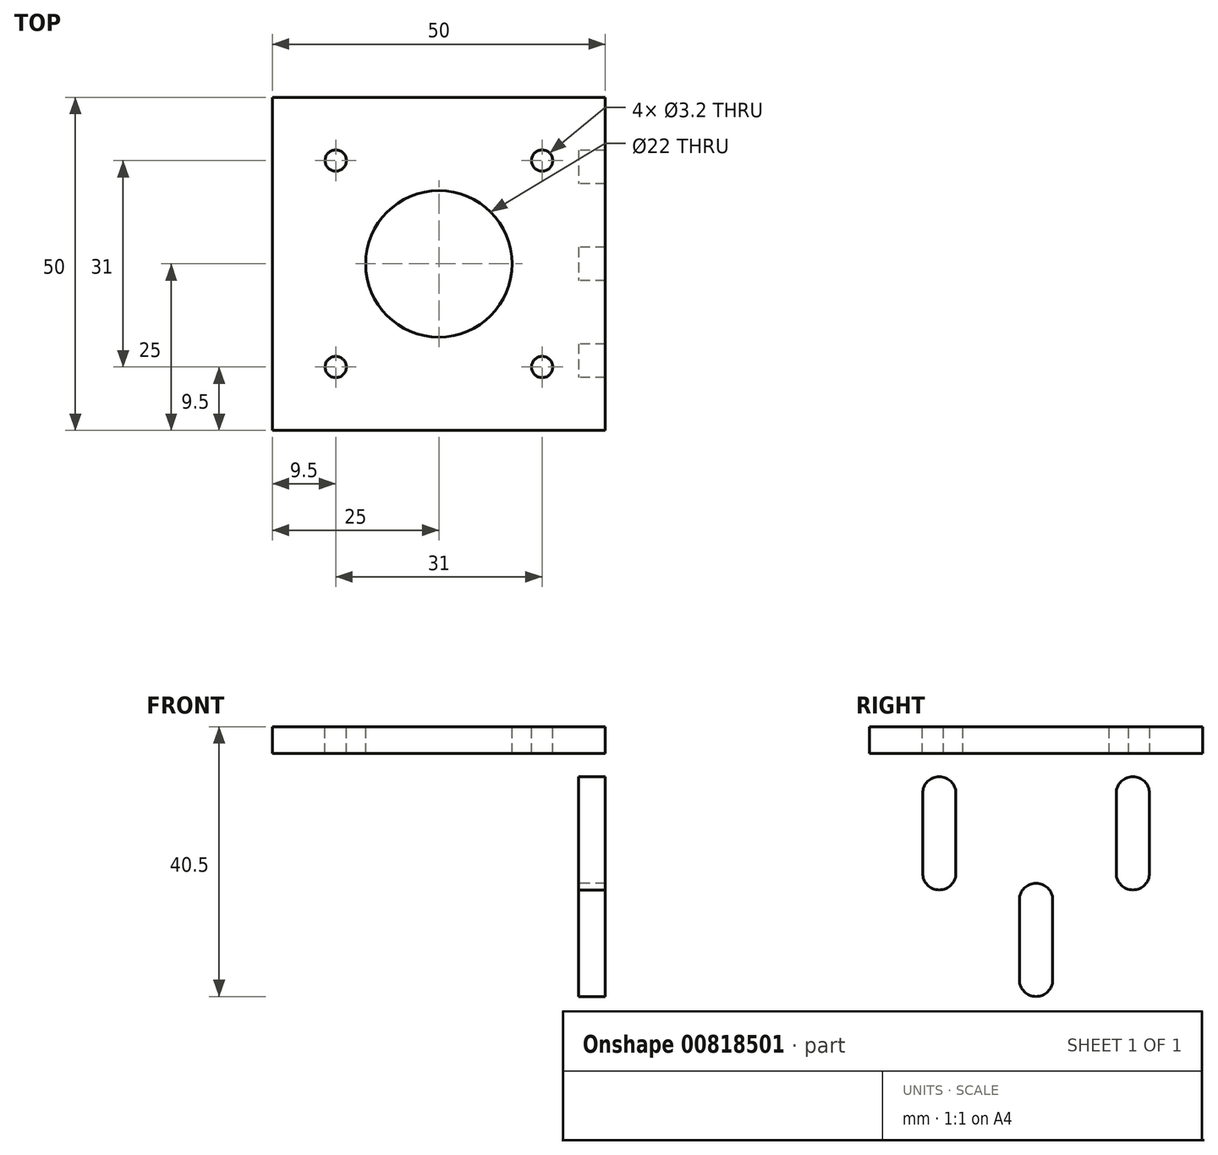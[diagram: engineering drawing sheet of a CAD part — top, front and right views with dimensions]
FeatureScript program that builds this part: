
annotation { "Feature Type Name" : "Feature", "Feature Type Description" : "" }
export const myFeature = defineFeature(function(context is Context, id is Id, definition is map)
    precondition{}
    {
        {
            var Q0;
            Q0=qCreatedBy(makeId("Front.planeOp"),FACE);
            var sketch = newSketch(context, id + "F0", { "sketchPlane" : qUnion([Q0])});
            skLineSegment(sketch, "E0.bottom", {"start": v(0, 0) * mm, "end": v(-50, 0) * mm});
            skLineSegment(sketch, "E0.top", {"start": v(0, -42) * mm, "end": v(-4, -42) * mm});
            skLineSegment(sketch, "E0.left", {"start": v(0, 0) * mm, "end": v(0, -42) * mm});
            skLineSegment(sketch, "E0.right", {"start": v(-50, 0) * mm, "end": v(-50, -4) * mm});
            skLineSegment(sketch, "E1.top", {"start": v(-50, -4) * mm, "end": v(-4, -4) * mm});
            skLineSegment(sketch, "E1.right", {"start": v(-4, -42) * mm, "end": v(-4, -4) * mm});
            skSolve(sketch);
        }
        {
            var Q0;
            Q0=makeQuery(id+"F0.imprint","IMPRINT",FACE,{"disambiguationData":[TD([[makeQuery(id+"F0.imprint","IMPRINT",EDGE,{"derivedFrom":sQuery(id+"F0.wireOp",EDGE,"E0.bottom")}),1.0]])]});
            extrude(context, id + "F1", {"entities" : qUnion([Q0]), "endBound" : BoundingType.SYMMETRIC, "depth" : 50 * mm});
        }
        {
            var Q0;
            Q0=makeQuery(id+"F1.opExtrude","SWEPT_FACE",FACE,{"disambiguationData":[OSD([sQuery(id+"F0.wireOp",EDGE,"E0.bottom")])]});
            var sketch = newSketch(context, id + "F2", { "sketchPlane" : qUnion([Q0])});
            skLineSegment(sketch, "E2", {"start": v(-50, 25) * mm, "end": v(0, -25) * mm, "construction": true});
            skLineSegment(sketch, "E3.bottom", {"start": v(-40.5, 15.5) * mm, "end": v(-9.5, 15.5) * mm, "construction": true});
            skLineSegment(sketch, "E3.top", {"start": v(-40.5, -15.5) * mm, "end": v(-9.5, -15.5) * mm, "construction": true});
            skLineSegment(sketch, "E3.left", {"start": v(-40.5, 15.5) * mm, "end": v(-40.5, -15.5) * mm, "construction": true});
            skLineSegment(sketch, "E3.right", {"start": v(-9.5, 15.5) * mm, "end": v(-9.5, -15.5) * mm, "construction": true});
            skPoint(sketch, "E3.middle", {"position": v(-25, 0) * mm});
            skSolve(sketch);
        }
        {
            var Q0;
            Q0=sQuery(id+"F2.wireOp",VERTEX,"E3.bottom.end");
            var Q1;
            Q1=sQuery(id+"F2.wireOp",VERTEX,"E3.top.end");
            var Q2;
            Q2=sQuery(id+"F2.wireOp",VERTEX,"E3.top.start");
            var Q3;
            Q3=sQuery(id+"F2.wireOp",VERTEX,"E3.bottom.start");
            var Q4;
            Q4=makeQuery(id+"F1.opExtrude","SWEPT_BODY",BODY,{"disambiguationData":[OSD([sQuery(id+"F0.wireOp",EDGE,"E0.bottom"),sQuery(id+"F0.wireOp",EDGE,"E0.top"),sQuery(id+"F0.wireOp",EDGE,"E0.left"),sQuery(id+"F0.wireOp",EDGE,"E0.right"),sQuery(id+"F0.wireOp",EDGE,"E1.top"),sQuery(id+"F0.wireOp",EDGE,"E1.right")])]});
            hole(context, id + "F3", {"style" : HoleStyle.SIMPLE, "endStyle" : HoleEndStyle.THROUGH, "holeDiameter" : 3.2 * mm, "tappedDepth" : 12 * mm, "tapClearance" : 3, "locations" : qUnion([Q0, Q1, Q2, Q3]), "scope" : qUnion([Q4]), "majorDiameter" : 5 * mm});
        }
        {
            var Q0;
            Q0=sQuery(id+"F2.wireOp",VERTEX,"E3.middle");
            var Q1;
            Q1=makeQuery(id+"F1.opExtrude","SWEPT_BODY",BODY,{"disambiguationData":[OSD([sQuery(id+"F0.wireOp",EDGE,"E0.bottom"),sQuery(id+"F0.wireOp",EDGE,"E0.top"),sQuery(id+"F0.wireOp",EDGE,"E0.left"),sQuery(id+"F0.wireOp",EDGE,"E0.right"),sQuery(id+"F0.wireOp",EDGE,"E1.top"),sQuery(id+"F0.wireOp",EDGE,"E1.right")])]});
            hole(context, id + "F4", {"style" : HoleStyle.SIMPLE, "endStyle" : HoleEndStyle.THROUGH, "holeDiameter" : 22 * mm, "tappedDepth" : 12 * mm, "tapClearance" : 3, "locations" : qUnion([Q0]), "scope" : qUnion([Q1]), "majorDiameter" : 5 * mm});
        }
        {
            var Q0;
            Q0=makeQuery(id+"F1.opExtrude","SWEPT_FACE",FACE,{"disambiguationData":[OSD([sQuery(id+"F0.wireOp",EDGE,"E1.right")])]});
            var sketch = newSketch(context, id + "F5", { "sketchPlane" : qUnion([Q0])});
            skLineSegment(sketch, "E4", {"start": v(0, -38) * mm, "end": v(0, -26) * mm, "construction": true});
            skLineSegment(sketch, "E5", {"start": v(-14.53, -22) * mm, "end": v(-14.53, -10) * mm, "construction": true});
            skLineSegment(sketch, "E6.MirrorCS", {"start": v(14.53, -22) * mm, "end": v(14.53, -10) * mm, "construction": true});
            skArc(sketch, "E7.0.startCap", {"start": v(2.5, -38) * mm, "mid": v(0, -40.5) * mm, "end": v(-2.5, -38) * mm});
            skArc(sketch, "E7.0.endCap", {"start": v(-2.5, -26) * mm, "mid": v(0, -23.5) * mm, "end": v(2.5, -26) * mm});
            skLineSegment(sketch, "E7.0.left", {"start": v(-2.5, -38) * mm, "end": v(-2.5, -26) * mm});
            skLineSegment(sketch, "E7.0.right", {"start": v(2.5, -38) * mm, "end": v(2.5, -26) * mm});
            skArc(sketch, "E7.1.startCap", {"start": v(-12.03, -22) * mm, "mid": v(-14.53, -24.5) * mm, "end": v(-17.03, -22) * mm});
            skArc(sketch, "E7.1.endCap", {"start": v(-17.03, -10) * mm, "mid": v(-14.53, -7.5) * mm, "end": v(-12.03, -10) * mm});
            skLineSegment(sketch, "E7.1.left", {"start": v(-17.03, -22) * mm, "end": v(-17.03, -10) * mm});
            skLineSegment(sketch, "E7.1.right", {"start": v(-12.03, -22) * mm, "end": v(-12.03, -10) * mm});
            skArc(sketch, "E7.2.startCap", {"start": v(17.03, -22) * mm, "mid": v(14.53, -24.5) * mm, "end": v(12.03, -22) * mm});
            skArc(sketch, "E7.2.endCap", {"start": v(12.03, -10) * mm, "mid": v(14.53, -7.5) * mm, "end": v(17.03, -10) * mm});
            skLineSegment(sketch, "E7.2.left", {"start": v(12.03, -22) * mm, "end": v(12.03, -10) * mm});
            skLineSegment(sketch, "E7.2.right", {"start": v(17.03, -22) * mm, "end": v(17.03, -10) * mm});
            skSolve(sketch);
        }
        {
            var Q0;
            Q0=makeQuery(id+"F5.imprint","IMPRINT",FACE,{"disambiguationData":[TD([[makeQuery(id+"F5.imprint","IMPRINT",EDGE,{"derivedFrom":sQuery(id+"F5.wireOp",EDGE,"E7.1.startCap")}),-1.0]])]});
            var Q1;
            Q1=makeQuery(id+"F5.imprint","IMPRINT",FACE,{"disambiguationData":[TD([[makeQuery(id+"F5.imprint","IMPRINT",EDGE,{"derivedFrom":sQuery(id+"F5.wireOp",EDGE,"E7.0.startCap")}),-1.0]])]});
            var Q2;
            Q2=makeQuery(id+"F5.imprint","IMPRINT",FACE,{"disambiguationData":[TD([[makeQuery(id+"F5.imprint","IMPRINT",EDGE,{"derivedFrom":sQuery(id+"F5.wireOp",EDGE,"E7.2.startCap")}),-1.0]])]});
            extrude(context, id + "F6", {"entities" : qUnion([Q0, Q1, Q2]), "operationType" : NewBodyOperationType.REMOVE, "endBound" : BoundingType.THROUGH_ALL, "oppositeDirection" : true, "depth" : 25 * mm});
        }
    });
